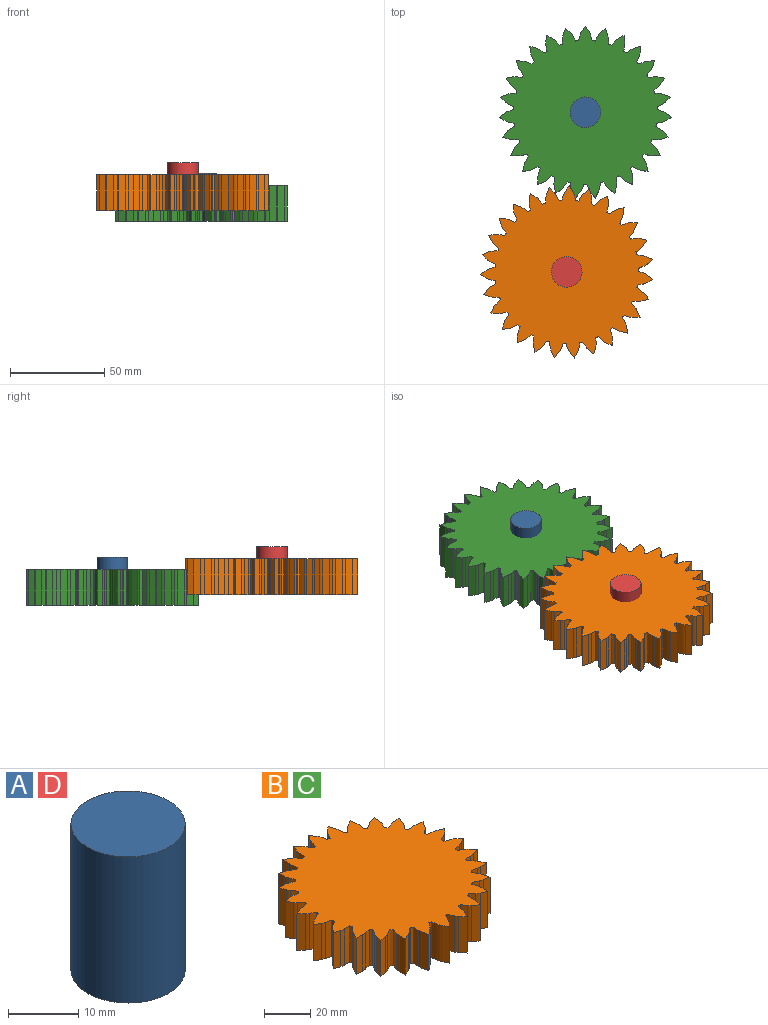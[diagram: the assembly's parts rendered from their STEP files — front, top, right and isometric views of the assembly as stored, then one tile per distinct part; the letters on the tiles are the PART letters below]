
ASSEMBLY  parts=4 mates=2
PART A: 3 faces, bbox 16.2x16.2x25.4 mm
  f0: cylinder r=8.11mm len=25.4mm, axis (0,0,-1), area 1294.6mm2, adj f1,f2
  f1: plane 16.22x16.22mm, normal (0,0,1), area 206.7mm2, adj f0
  f2: plane 16.22x16.22mm, normal (0,0,-1), area 206.7mm2, adj f0
PART B: 191 faces, bbox 91.3x91.1x19.1 mm
  f0: plane 19.05x3.59mm, normal (-1,-0.01,0), area 68.4mm2, adj f1,f188,f189,f190
  f1: plane 19.05x3.31mm, normal (0.39,-0.92,0), area 68.4mm2, adj f0,f2,f189,f190
  f2: cylinder r=6.35mm len=19.05mm, axis (0,0,-1), area 37.2mm2, adj f1,f3,f189,f190
  f3: plane 19.05x2.4mm, normal (0.65,-0.76,0), area 60.3mm2, adj f2,f4,f189,f190
  f4: cylinder r=38.1mm len=19.05mm, axis (0,0,-1), area 28.4mm2, adj f3,f5,f189,f190
  f5: plane 19.05x3.16mm, normal (-1,0.07,0), area 60.3mm2, adj f4,f6,f189,f190
  f6: cylinder r=6.35mm len=19.05mm, axis (0,0,-1), area 37.2mm2, adj f5,f7,f189,f190
  f7: plane 19.05x3.49mm, normal (-0.97,-0.24,0), area 68.4mm2, adj f6,f8,f189,f190
  f8: plane 19.05x2.89mm, normal (0.59,-0.81,0), area 68.4mm2, adj f7,f9,f189,f190
  f9: cylinder r=6.35mm len=19.05mm, axis (0,0,-1), area 37.2mm2, adj f8,f10,f189,f190
  f10: plane 19.05x2.56mm, normal (0.81,-0.59,0), area 60.3mm2, adj f9,f11,f189,f190
  f11: cylinder r=38.1mm len=19.05mm, axis (0,0,-1), area 28.4mm2, adj f10,f12,f189,f190
  f12: plane 19.05x3.12mm, normal (-0.99,-0.16,0), area 60.3mm2, adj f11,f13,f189,f190
  f13: cylinder r=6.35mm len=19.05mm, axis (0,0,-1), area 37.2mm2, adj f12,f14,f189,f190
  f14: plane 19.05x3.2mm, normal (-0.89,-0.45,0), area 68.4mm2, adj f13,f15,f189,f190
  f15: plane 19.05x2.74mm, normal (0.76,-0.65,0), area 68.4mm2, adj f14,f16,f189,f190
  f16: cylinder r=6.35mm len=19.05mm, axis (0,0,-1), area 37.2mm2, adj f15,f17,f189,f190
  f17: plane 19.05x2.92mm, normal (0.92,-0.39,0), area 60.3mm2, adj f16,f18,f189,f190
  f18: cylinder r=38.1mm len=19.05mm, axis (0,0,-1), area 28.4mm2, adj f17,f19,f189,f190
  f19: plane 19.05x2.92mm, normal (-0.92,-0.39,0), area 60.3mm2, adj f18,f20,f189,f190
  f20: cylinder r=6.35mm len=19.05mm, axis (0,0,-1), area 37.2mm2, adj f19,f21,f189,f190
  f21: plane 19.05x2.74mm, normal (-0.76,-0.65,0), area 68.4mm2, adj f20,f22,f189,f190
  f22: plane 19.05x3.2mm, normal (0.89,-0.45,0), area 68.4mm2, adj f21,f23,f189,f190
  f23: cylinder r=6.35mm len=19.05mm, axis (0,0,-1), area 37.2mm2, adj f22,f24,f189,f190
  f24: plane 19.05x3.12mm, normal (0.99,-0.16,0), area 60.3mm2, adj f23,f25,f189,f190
  f25: cylinder r=38.1mm len=19.05mm, axis (0,0,-1), area 28.4mm2, adj f24,f26,f189,f190
  f26: plane 19.05x2.56mm, normal (-0.81,-0.59,0), area 60.3mm2, adj f25,f27,f189,f190
  f27: cylinder r=6.35mm len=19.05mm, axis (0,0,-1), area 37.2mm2, adj f26,f28,f189,f190
  f28: plane 19.05x2.89mm, normal (-0.59,-0.81,0), area 68.4mm2, adj f27,f29,f189,f190
  f29: plane 19.05x3.49mm, normal (0.97,-0.24,0), area 68.4mm2, adj f28,f30,f189,f190
  f30: cylinder r=6.35mm len=19.05mm, axis (0,0,-1), area 37.2mm2, adj f29,f31,f189,f190
  f31: plane 19.05x3.16mm, normal (1,0.07,0), area 60.3mm2, adj f30,f32,f189,f190
  f32: cylinder r=38.1mm len=19.05mm, axis (0,0,-1), area 28.4mm2, adj f31,f33,f189,f190
  f33: plane 19.05x2.4mm, normal (-0.65,-0.76,0), area 60.3mm2, adj f32,f34,f189,f190
  f34: cylinder r=6.35mm len=19.05mm, axis (0,0,-1), area 37.2mm2, adj f33,f35,f189,f190
  f35: plane 19.05x3.31mm, normal (-0.39,-0.92,0), area 68.4mm2, adj f34,f36,f189,f190
  f36: plane 19.05x3.59mm, normal (1,-0.01,0), area 68.4mm2, adj f35,f37,f189,f190
  f37: cylinder r=6.35mm len=19.05mm, axis (0,0,-1), area 37.2mm2, adj f36,f38,f189,f190
  f38: plane 19.05x3.02mm, normal (0.95,0.3,0), area 60.3mm2, adj f37,f39,f189,f190
  f39: cylinder r=38.1mm len=19.05mm, axis (0,0,-1), area 28.4mm2, adj f38,f40,f189,f190
  f40: plane 19.05x2.81mm, normal (-0.46,-0.89,0), area 60.3mm2, adj f39,f41,f189,f190
  f41: cylinder r=6.35mm len=19.05mm, axis (0,0,-1), area 37.2mm2, adj f40,f42,f189,f190
  f42: plane 19.05x3.54mm, normal (-0.17,-0.99,0), area 68.4mm2, adj f41,f43,f189,f190
  f43: plane 19.05x3.5mm, normal (0.97,0.23,0), area 68.4mm2, adj f42,f44,f189,f190
  f44: cylinder r=6.35mm len=19.05mm, axis (0,0,-1), area 37.2mm2, adj f43,f45,f189,f190
  f45: plane 19.05x2.72mm, normal (0.86,0.51,0), area 60.3mm2, adj f44,f46,f189,f190
  f46: cylinder r=38.1mm len=19.05mm, axis (0,0,-1), area 28.4mm2, adj f45,f47,f189,f190
  f47: plane 19.05x3.07mm, normal (-0.24,-0.97,0), area 60.3mm2, adj f46,f48,f189,f190
  f48: cylinder r=6.35mm len=19.05mm, axis (0,0,-1), area 37.2mm2, adj f47,f49,f189,f190
  f49: plane 19.05x3.59mm, normal (0.06,-1,0), area 68.4mm2, adj f48,f50,f189,f190
  f50: plane 19.05x3.22mm, normal (0.9,0.44,0), area 68.4mm2, adj f49,f51,f189,f190
  f51: cylinder r=6.35mm len=19.05mm, axis (0,0,-1), area 37.2mm2, adj f50,f52,f189,f190
  f52: plane 19.05x2.28mm, normal (0.72,0.69,0), area 60.3mm2, adj f51,f53,f189,f190
  f53: cylinder r=38.1mm len=19.05mm, axis (0,0,-1), area 28.4mm2, adj f52,f54,f189,f190
  f54: plane 19.05x3.17mm, normal (-0.01,-1,0), area 60.3mm2, adj f53,f55,f189,f190
  f55: cylinder r=6.35mm len=19.05mm, axis (0,0,-1), area 37.2mm2, adj f54,f56,f189,f190
  f56: plane 19.05x3.44mm, normal (0.29,-0.96,0), area 68.4mm2, adj f55,f57,f189,f190
  f57: plane 19.05x2.76mm, normal (0.77,0.64,0), area 68.4mm2, adj f56,f58,f189,f190
  f58: cylinder r=6.35mm len=19.05mm, axis (0,0,-1), area 37.2mm2, adj f57,f59,f189,f190
  f59: plane 19.05x2.66mm, normal (0.54,0.84,0), area 60.3mm2, adj f58,f60,f189,f190
  f60: cylinder r=38.1mm len=19.05mm, axis (0,0,-1), area 28.4mm2, adj f59,f61,f189,f190
  f61: plane 19.05x3.09mm, normal (0.22,-0.98,0), area 60.3mm2, adj f60,f62,f189,f190
  f62: cylinder r=6.35mm len=19.05mm, axis (0,0,-1), area 37.2mm2, adj f61,f63,f189,f190
  f63: plane 19.05x3.1mm, normal (0.5,-0.86,0), area 68.4mm2, adj f62,f64,f189,f190
  f64: plane 19.05x2.87mm, normal (0.6,0.8,0), area 68.4mm2, adj f63,f65,f189,f190
  f65: cylinder r=6.35mm len=19.05mm, axis (0,0,-1), area 37.2mm2, adj f64,f66,f189,f190
  f66: plane 19.05x2.99mm, normal (0.33,0.94,0), area 60.3mm2, adj f65,f67,f189,f190
  f67: cylinder r=38.1mm len=19.05mm, axis (0,0,-1), area 28.4mm2, adj f66,f68,f189,f190
  f68: plane 19.05x2.84mm, normal (0.44,-0.9,0), area 60.3mm2, adj f67,f69,f189,f190
  f69: cylinder r=6.35mm len=19.05mm, axis (0,0,-1), area 37.2mm2, adj f68,f70,f189,f190
  f70: plane 19.05x2.6mm, normal (0.69,-0.72,0), area 68.4mm2, adj f69,f71,f189,f190
  f71: plane 19.05x3.29mm, normal (0.4,0.92,0), area 68.4mm2, adj f70,f72,f189,f190
  f72: cylinder r=6.35mm len=19.05mm, axis (0,0,-1), area 37.2mm2, adj f71,f73,f189,f190
  f73: plane 19.05x3.15mm, normal (0.1,0.99,0), area 60.3mm2, adj f72,f74,f189,f190
  f74: cylinder r=38.1mm len=19.05mm, axis (0,0,-1), area 28.4mm2, adj f73,f75,f189,f190
  f75: plane 19.05x2.45mm, normal (0.63,-0.77,0), area 60.3mm2, adj f74,f76,f189,f190
  f76: cylinder r=6.35mm len=19.05mm, axis (0,0,-1), area 37.2mm2, adj f75,f77,f189,f190
  f77: plane 19.05x3.01mm, normal (0.84,-0.54,0), area 68.4mm2, adj f76,f78,f189,f190
  f78: plane 19.05x3.53mm, normal (0.18,0.98,0), area 68.4mm2, adj f77,f79,f189,f190
  f79: cylinder r=6.35mm len=19.05mm, axis (0,0,-1), area 37.2mm2, adj f78,f80,f189,f190
  f80: plane 19.05x3.14mm, normal (-0.13,0.99,0), area 60.3mm2, adj f79,f81,f189,f190
  f81: cylinder r=38.1mm len=19.05mm, axis (0,0,-1), area 28.4mm2, adj f80,f82,f189,f190
  f82: plane 19.05x2.52mm, normal (0.8,-0.61,0), area 60.3mm2, adj f81,f83,f189,f190
  f83: cylinder r=6.35mm len=19.05mm, axis (0,0,-1), area 37.2mm2, adj f82,f84,f189,f190
  f84: plane 19.05x3.38mm, normal (0.94,-0.34,0), area 68.4mm2, adj f83,f85,f189,f190
  f85: plane 19.05x3.59mm, normal (-0.05,1,0), area 68.4mm2, adj f84,f86,f189,f190
  f86: cylinder r=6.35mm len=19.05mm, axis (0,0,-1), area 37.2mm2, adj f85,f87,f189,f190
  f87: plane 19.05x2.96mm, normal (-0.35,0.94,0), area 60.3mm2, adj f86,f88,f189,f190
  f88: cylinder r=38.1mm len=19.05mm, axis (0,0,-1), area 28.4mm2, adj f87,f89,f189,f190
  f89: plane 19.05x2.89mm, normal (0.91,-0.41,0), area 60.3mm2, adj f88,f90,f189,f190
  f90: cylinder r=6.35mm len=19.05mm, axis (0,0,-1), area 37.2mm2, adj f89,f91,f189,f190
  f91: plane 19.05x3.57mm, normal (0.99,-0.11,0), area 68.4mm2, adj f90,f92,f189,f190
  f92: plane 19.05x3.45mm, normal (-0.28,0.96,0), area 68.4mm2, adj f91,f93,f189,f190
  f93: cylinder r=6.35mm len=19.05mm, axis (0,0,-1), area 37.2mm2, adj f92,f94,f189,f190
  f94: plane 19.05x2.63mm, normal (-0.56,0.83,0), area 60.3mm2, adj f93,f95,f189,f190
  f95: cylinder r=38.1mm len=19.05mm, axis (0,0,-1), area 28.4mm2, adj f94,f96,f189,f190
  f96: plane 19.05x3.11mm, normal (0.98,-0.18,0), area 60.3mm2, adj f95,f97,f189,f190
  f97: cylinder r=6.35mm len=19.05mm, axis (0,0,-1), area 37.2mm2, adj f96,f98,f189,f190
  f98: plane 19.05x3.57mm, normal (0.99,0.12,0), area 68.4mm2, adj f97,f99,f189,f190
  f99: plane 19.05x3.12mm, normal (-0.5,0.87,0), area 68.4mm2, adj f98,f100,f189,f190
  f100: cylinder r=6.35mm len=19.05mm, axis (0,0,-1), area 37.2mm2, adj f99,f101,f189,f190
  f101: plane 19.05x2.33mm, normal (-0.74,0.68,0), area 60.3mm2, adj f100,f102,f189,f190
  f102: cylinder r=38.1mm len=19.05mm, axis (0,0,-1), area 28.4mm2, adj f101,f103,f189,f190
  f103: plane 19.05x3.16mm, normal (1,0.05,0), area 60.3mm2, adj f102,f104,f189,f190
  f104: cylinder r=6.35mm len=19.05mm, axis (0,0,-1), area 37.2mm2, adj f103,f105,f189,f190
  f105: plane 19.05x3.37mm, normal (0.94,0.35,0), area 68.4mm2, adj f104,f106,f189,f190
  f106: plane 19.05x2.63mm, normal (-0.68,0.73,0), area 68.4mm2, adj f105,f107,f189,f190
  f107: cylinder r=6.35mm len=19.05mm, axis (0,0,-1), area 37.2mm2, adj f106,f108,f189,f190
  f108: plane 19.05x2.76mm, normal (-0.87,0.49,0), area 60.3mm2, adj f107,f109,f189,f190
  f109: cylinder r=38.1mm len=19.05mm, axis (0,0,-1), area 28.4mm2, adj f108,f110,f189,f190
  f110: plane 19.05x3.04mm, normal (0.96,0.28,0), area 60.3mm2, adj f109,f111,f189,f190
  f111: cylinder r=6.35mm len=19.05mm, axis (0,0,-1), area 37.2mm2, adj f110,f112,f189,f190
  f112: plane 19.05x2.99mm, normal (0.83,0.55,0), area 68.4mm2, adj f111,f113,f189,f190
  f113: plane 19.05x2.99mm, normal (-0.83,0.55,0), area 68.4mm2, adj f112,f114,f189,f190
  f114: cylinder r=6.35mm len=19.05mm, axis (0,0,-1), area 37.2mm2, adj f113,f115,f189,f190
  f115: plane 19.05x3.04mm, normal (-0.96,0.28,0), area 60.3mm2, adj f114,f116,f189,f190
  f116: cylinder r=38.1mm len=19.05mm, axis (0,0,-1), area 28.4mm2, adj f115,f117,f189,f190
  f117: plane 19.05x2.76mm, normal (0.87,0.49,0), area 60.3mm2, adj f116,f118,f189,f190
  f118: cylinder r=6.35mm len=19.05mm, axis (0,0,-1), area 37.2mm2, adj f117,f119,f189,f190
  f119: plane 19.05x2.63mm, normal (0.68,0.73,0), area 68.4mm2, adj f118,f120,f189,f190
  f120: plane 19.05x3.37mm, normal (-0.94,0.35,0), area 68.4mm2, adj f119,f121,f189,f190
  f121: cylinder r=6.35mm len=19.05mm, axis (0,0,-1), area 37.2mm2, adj f120,f122,f189,f190
  f122: plane 19.05x3.16mm, normal (-1,0.05,0), area 60.3mm2, adj f121,f123,f189,f190
  f123: cylinder r=38.1mm len=19.05mm, axis (0,0,-1), area 28.4mm2, adj f122,f124,f189,f190
  f124: plane 19.05x2.33mm, normal (0.74,0.68,0), area 60.3mm2, adj f123,f125,f189,f190
  f125: cylinder r=6.35mm len=19.05mm, axis (0,0,-1), area 37.2mm2, adj f124,f126,f189,f190
  f126: plane 19.05x3.12mm, normal (0.5,0.87,0), area 68.4mm2, adj f125,f127,f189,f190
  f127: plane 19.05x3.57mm, normal (-0.99,0.12,0), area 68.4mm2, adj f126,f128,f189,f190
  f128: cylinder r=6.35mm len=19.05mm, axis (0,0,-1), area 37.2mm2, adj f127,f129,f189,f190
  f129: plane 19.05x3.11mm, normal (-0.98,-0.18,0), area 60.3mm2, adj f128,f130,f189,f190
  f130: cylinder r=38.1mm len=19.05mm, axis (0,0,-1), area 28.4mm2, adj f129,f131,f189,f190
  f131: plane 19.05x2.63mm, normal (0.56,0.83,0), area 60.3mm2, adj f130,f132,f189,f190
  f132: cylinder r=6.35mm len=19.05mm, axis (0,0,-1), area 37.2mm2, adj f131,f133,f189,f190
  f133: plane 19.05x3.45mm, normal (0.28,0.96,0), area 68.4mm2, adj f132,f134,f189,f190
  f134: plane 19.05x3.57mm, normal (-0.99,-0.11,0), area 68.4mm2, adj f133,f135,f189,f190
  f135: cylinder r=6.35mm len=19.05mm, axis (0,0,-1), area 37.2mm2, adj f134,f136,f189,f190
  f136: plane 19.05x2.89mm, normal (-0.91,-0.41,0), area 60.3mm2, adj f135,f137,f189,f190
  f137: cylinder r=38.1mm len=19.05mm, axis (0,0,-1), area 28.4mm2, adj f136,f138,f189,f190
  f138: plane 19.05x2.96mm, normal (0.35,0.94,0), area 60.3mm2, adj f137,f139,f189,f190
  f139: cylinder r=6.35mm len=19.05mm, axis (0,0,-1), area 37.2mm2, adj f138,f140,f189,f190
  f140: plane 19.05x3.59mm, normal (0.05,1,0), area 68.4mm2, adj f139,f141,f189,f190
  f141: plane 19.05x3.38mm, normal (-0.94,-0.34,0), area 68.4mm2, adj f140,f142,f189,f190
  f142: cylinder r=6.35mm len=19.05mm, axis (0,0,-1), area 37.2mm2, adj f141,f143,f189,f190
  f143: plane 19.05x2.52mm, normal (-0.8,-0.61,0), area 60.3mm2, adj f142,f144,f189,f190
  f144: cylinder r=38.1mm len=19.05mm, axis (0,0,-1), area 28.4mm2, adj f143,f145,f189,f190
  f145: plane 19.05x3.14mm, normal (0.13,0.99,0), area 60.3mm2, adj f144,f146,f189,f190
  f146: cylinder r=6.35mm len=19.05mm, axis (0,0,-1), area 37.2mm2, adj f145,f147,f189,f190
  f147: plane 19.05x3.53mm, normal (-0.18,0.98,0), area 68.4mm2, adj f146,f148,f189,f190
  f148: plane 19.05x3.01mm, normal (-0.84,-0.54,0), area 68.4mm2, adj f147,f149,f189,f190
  f149: cylinder r=6.35mm len=19.05mm, axis (0,0,-1), area 37.2mm2, adj f148,f150,f189,f190
  f150: plane 19.05x2.45mm, normal (-0.63,-0.77,0), area 60.3mm2, adj f149,f151,f189,f190
  f151: cylinder r=38.1mm len=19.05mm, axis (0,0,-1), area 28.4mm2, adj f150,f152,f189,f190
  f152: plane 19.05x3.15mm, normal (-0.1,0.99,0), area 60.3mm2, adj f151,f153,f189,f190
  f153: cylinder r=6.35mm len=19.05mm, axis (0,0,-1), area 37.2mm2, adj f152,f154,f189,f190
  f154: plane 19.05x3.29mm, normal (-0.4,0.92,0), area 68.4mm2, adj f153,f155,f189,f190
  f155: plane 19.05x2.6mm, normal (-0.69,-0.72,0), area 68.4mm2, adj f154,f156,f189,f190
  f156: cylinder r=6.35mm len=19.05mm, axis (0,0,-1), area 37.2mm2, adj f155,f157,f189,f190
  f157: plane 19.05x2.84mm, normal (-0.44,-0.9,0), area 60.3mm2, adj f156,f158,f189,f190
  f158: cylinder r=38.1mm len=19.05mm, axis (0,0,-1), area 28.4mm2, adj f157,f159,f189,f190
  f159: plane 19.05x2.99mm, normal (-0.33,0.94,0), area 60.3mm2, adj f158,f160,f189,f190
  f160: cylinder r=6.35mm len=19.05mm, axis (0,0,-1), area 37.2mm2, adj f159,f161,f189,f190
  f161: plane 19.05x2.87mm, normal (-0.6,0.8,0), area 68.4mm2, adj f160,f162,f189,f190
  f162: plane 19.05x3.1mm, normal (-0.5,-0.86,0), area 68.4mm2, adj f161,f163,f189,f190
  f163: cylinder r=6.35mm len=19.05mm, axis (0,0,-1), area 37.2mm2, adj f162,f164,f189,f190
  f164: plane 19.05x3.09mm, normal (-0.22,-0.98,0), area 60.3mm2, adj f163,f165,f189,f190
  f165: cylinder r=38.1mm len=19.05mm, axis (0,0,-1), area 28.4mm2, adj f164,f166,f189,f190
  f166: plane 19.05x2.66mm, normal (-0.54,0.84,0), area 60.3mm2, adj f165,f167,f189,f190
  f167: cylinder r=6.35mm len=19.05mm, axis (0,0,-1), area 37.2mm2, adj f166,f168,f189,f190
  f168: plane 19.05x2.76mm, normal (-0.77,0.64,0), area 68.4mm2, adj f167,f169,f189,f190
  f169: plane 19.05x3.44mm, normal (-0.29,-0.96,0), area 68.4mm2, adj f168,f170,f189,f190
  f170: cylinder r=6.35mm len=19.05mm, axis (0,0,-1), area 37.2mm2, adj f169,f171,f189,f190
  f171: plane 19.05x3.17mm, normal (0.01,-1,0), area 60.3mm2, adj f170,f172,f189,f190
  f172: cylinder r=38.1mm len=19.05mm, axis (0,0,-1), area 28.4mm2, adj f171,f173,f189,f190
  f173: plane 19.05x2.28mm, normal (-0.72,0.69,0), area 60.3mm2, adj f172,f174,f189,f190
  f174: cylinder r=6.35mm len=19.05mm, axis (0,0,-1), area 37.2mm2, adj f173,f175,f189,f190
  f175: plane 19.05x3.22mm, normal (-0.9,0.44,0), area 68.4mm2, adj f174,f176,f189,f190
  f176: plane 19.05x3.59mm, normal (-0.06,-1,0), area 68.4mm2, adj f175,f177,f189,f190
  f177: cylinder r=6.35mm len=19.05mm, axis (0,0,-1), area 37.2mm2, adj f176,f178,f189,f190
  f178: plane 19.05x3.07mm, normal (0.24,-0.97,0), area 60.3mm2, adj f177,f179,f189,f190
  f179: cylinder r=38.1mm len=19.05mm, axis (0,0,-1), area 28.4mm2, adj f178,f180,f189,f190
  f180: plane 19.05x2.72mm, normal (-0.86,0.51,0), area 60.3mm2, adj f179,f181,f189,f190
  f181: cylinder r=6.35mm len=19.05mm, axis (0,0,-1), area 37.2mm2, adj f180,f182,f189,f190
  f182: plane 19.05x3.5mm, normal (-0.97,0.23,0), area 68.4mm2, adj f181,f183,f189,f190
  f183: plane 19.05x3.54mm, normal (0.17,-0.99,0), area 68.4mm2, adj f182,f184,f189,f190
  f184: cylinder r=6.35mm len=19.05mm, axis (0,0,-1), area 37.2mm2, adj f183,f185,f189,f190
  f185: plane 19.05x2.81mm, normal (0.46,-0.89,0), area 60.3mm2, adj f184,f186,f189,f190
  f186: cylinder r=38.1mm len=19.05mm, axis (0,0,-1), area 28.4mm2, adj f185,f187,f189,f190
  f187: plane 19.05x3.02mm, normal (-0.95,0.3,0), area 60.3mm2, adj f186,f188,f189,f190
  f188: cylinder r=6.35mm len=19.05mm, axis (0,0,-1), area 37.2mm2, adj f0,f187,f189,f190
  f189: plane 91.29x91.13mm, normal (0,0,1), area 5464.4mm2, adj f0,f1,f2,f3,f4,f5,f6,f7
  f190: plane 91.29x91.13mm, normal (0,0,-1), area 5464.4mm2, adj f0,f1,f2,f3,f4,f5,f6,f7
PART C: same geometry as B
PART D: same geometry as A
PLACE A t=(96.82,133.82,3.11)mm
PLACE B rot(axis=(0,0,-1),15deg) t=(2.18,80.61,8.87)mm
PLACE C t=(12.02,165.22,3.11)mm
PLACE D rot(axis=(0,0,-1),15deg) t=(75.96,28.34,8.87)mm
MATE revolute B.f53 <-> D.f0  axis (0,0,-1) through (2.18,80.61,8.87)mm
MATE revolute C.f53 <-> A.f0  axis (0,0,-1) through (12.02,165.22,3.11)mm
